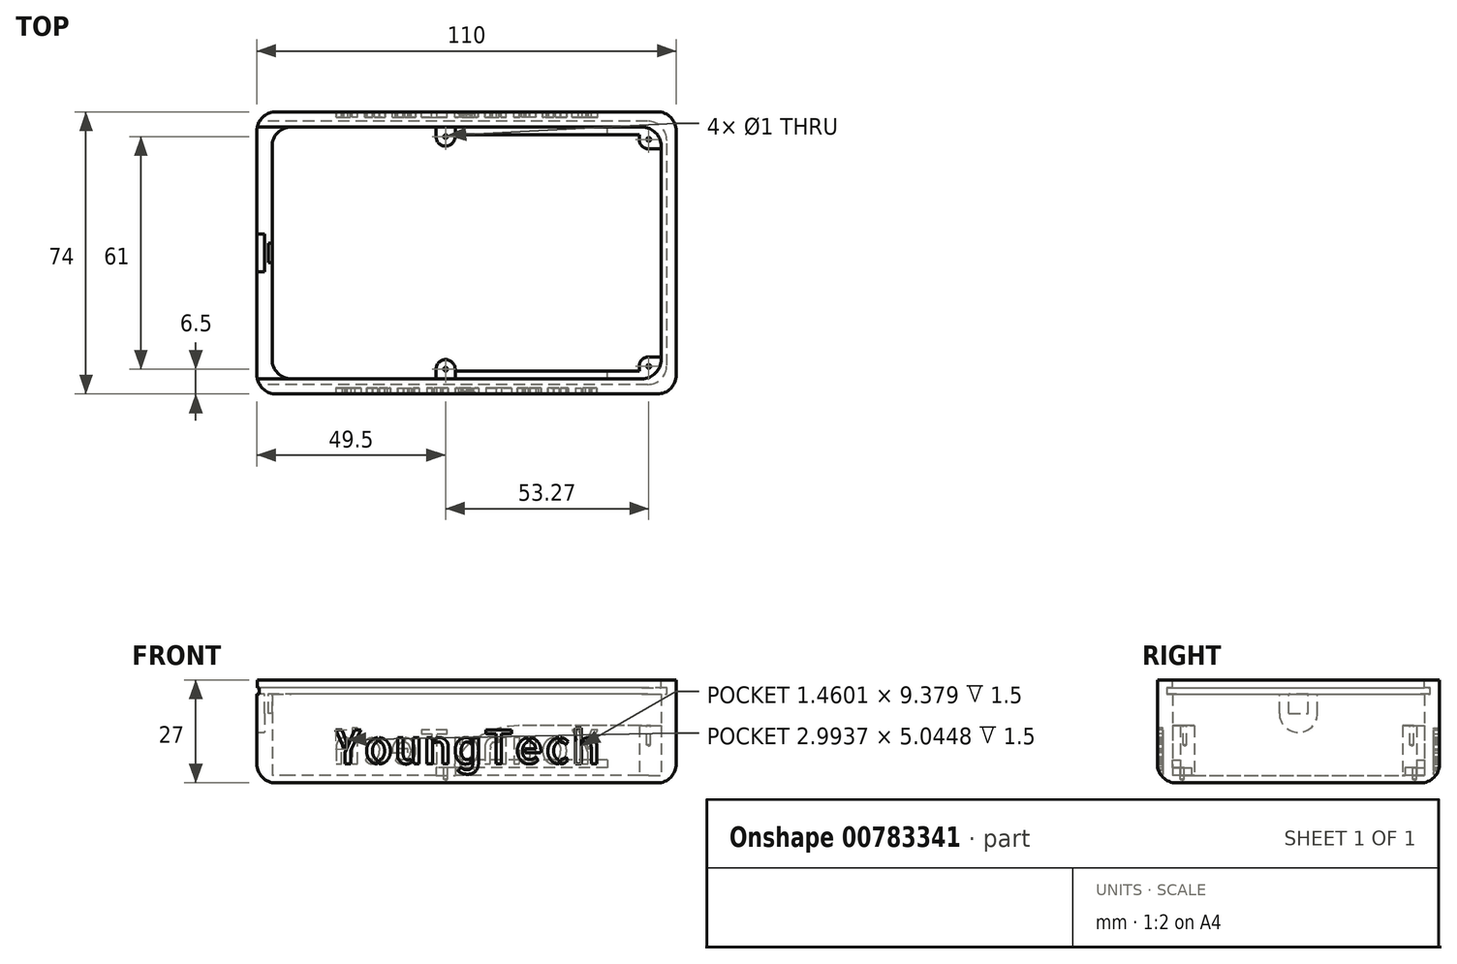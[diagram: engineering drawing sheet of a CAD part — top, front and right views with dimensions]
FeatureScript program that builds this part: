
annotation { "Feature Type Name" : "Feature", "Feature Type Description" : "" }
export const myFeature = defineFeature(function(context is Context, id is Id, definition is map)
    precondition{}
    {
        {
            var Q0;
            Q0=qCreatedBy(makeId("Top.planeOp"),FACE);
            var sketch = newSketch(context, id + "F0", { "sketchPlane" : qUnion([Q0])});
            skLineSegment(sketch, "E0.bottom", {"start": v(55, -37) * mm, "end": v(-55, -37) * mm});
            skLineSegment(sketch, "E0.top", {"start": v(55, 37) * mm, "end": v(-55, 37) * mm});
            skLineSegment(sketch, "E0.left", {"start": v(55, -37) * mm, "end": v(55, 37) * mm});
            skLineSegment(sketch, "E0.right", {"start": v(-55, -37) * mm, "end": v(-55, 37) * mm});
            skPoint(sketch, "E0.middle", {"position": v(0, 0) * mm});
            skSolve(sketch);
        }
        {
            var Q0;
            Q0 = qSketchRegion(id + "F0", true);
            extrude(context, id + "F1", {"entities" : qUnion([Q0]), "depth" : 2 * mm, "offsetDistance" : 25 * mm});
        }
        {
            var Q0;
            Q0=makeQuery(id+"F1.opExtrude","CAP_FACE",FACE,{"disambiguationData":[OSD([sQuery(id+"F0.wireOp",EDGE,"E0.bottom"),sQuery(id+"F0.wireOp",EDGE,"E0.top"),sQuery(id+"F0.wireOp",EDGE,"E0.left"),sQuery(id+"F0.wireOp",EDGE,"E0.right")])],"isStart":false});
            var sketch = newSketch(context, id + "F2", { "sketchPlane" : qUnion([Q0])});
            skLineSegment(sketch, "E1.0.0", {"start": v(55, 37) * mm, "end": v(55, -37) * mm});
            skLineSegment(sketch, "E1.0.1", {"start": v(55, -37) * mm, "end": v(-55, -37) * mm});
            skLineSegment(sketch, "E1.0.2", {"start": v(-55, -37) * mm, "end": v(-55, 37) * mm});
            skLineSegment(sketch, "E1.0.3", {"start": v(-55, 37) * mm, "end": v(55, 37) * mm});
            skLineSegment(sketch, "E2.bottom", {"start": v(51, -33) * mm, "end": v(-51, -33) * mm});
            skLineSegment(sketch, "E2.top", {"start": v(51, 33) * mm, "end": v(-51, 33) * mm});
            skLineSegment(sketch, "E2.left", {"start": v(51, -33) * mm, "end": v(51, 33) * mm});
            skLineSegment(sketch, "E2.right", {"start": v(-51, -33) * mm, "end": v(-51, 33) * mm});
            skPoint(sketch, "E2.middle", {"position": v(0, 0) * mm});
            skSolve(sketch);
        }
        {
            var Q0;
            Q0=makeQuery(id+"F2.imprint","IMPRINT",FACE,{"disambiguationData":[TD([[makeQuery(id+"F2.imprint","IMPRINT",EDGE,{"derivedFrom":sQuery(id+"F2.wireOp",EDGE,"E1.0.0")}),1.0]])]});
            extrude(context, id + "F3", {"entities" : qUnion([Q0]), "operationType" : NewBodyOperationType.ADD, "depth" : 25 * mm, "offsetDistance" : 25 * mm});
        }
        {
            var Q0;
            Q0=makeQuery(id+"F3.boolean.opBoolean","MERGE",EDGE,{"derivedFrom":[makeQuery(id+"F1.opExtrude","SWEPT_EDGE",EDGE,{"disambiguationData":[OSD([sQuery(id+"F0.wireOp",EDGE,"E0.top"),sQuery(id+"F0.wireOp",EDGE,"E0.right")])]}),makeQuery(id+"F3.opExtrude","SWEPT_EDGE",EDGE,{"disambiguationData":[OSD([sQuery(id+"F2.wireOp",EDGE,"E1.0.2"),sQuery(id+"F2.wireOp",EDGE,"E1.0.3")])]})]});
            var Q1;
            Q1=makeQuery(id+"F3.boolean.opBoolean","MERGE",EDGE,{"derivedFrom":[makeQuery(id+"F1.opExtrude","SWEPT_EDGE",EDGE,{"disambiguationData":[OSD([sQuery(id+"F0.wireOp",EDGE,"E0.bottom"),sQuery(id+"F0.wireOp",EDGE,"E0.right")])]}),makeQuery(id+"F3.opExtrude","SWEPT_EDGE",EDGE,{"disambiguationData":[OSD([sQuery(id+"F2.wireOp",EDGE,"E1.0.1"),sQuery(id+"F2.wireOp",EDGE,"E1.0.2")])]})]});
            var Q2;
            Q2=makeQuery(id+"F3.boolean.opBoolean","MERGE",EDGE,{"derivedFrom":[makeQuery(id+"F1.opExtrude","SWEPT_EDGE",EDGE,{"disambiguationData":[OSD([sQuery(id+"F0.wireOp",EDGE,"E0.bottom"),sQuery(id+"F0.wireOp",EDGE,"E0.left")])]}),makeQuery(id+"F3.opExtrude","SWEPT_EDGE",EDGE,{"disambiguationData":[OSD([sQuery(id+"F2.wireOp",EDGE,"E1.0.0"),sQuery(id+"F2.wireOp",EDGE,"E1.0.1")])]})]});
            var Q3;
            Q3=makeQuery(id+"F3.opExtrude","SWEPT_EDGE",EDGE,{"disambiguationData":[OSD([sQuery(id+"F2.wireOp",EDGE,"E2.top"),sQuery(id+"F2.wireOp",EDGE,"E2.left")])]});
            var Q4;
            Q4=makeQuery(id+"F3.boolean.opBoolean","MERGE",EDGE,{"derivedFrom":[makeQuery(id+"F1.opExtrude","SWEPT_EDGE",EDGE,{"disambiguationData":[OSD([sQuery(id+"F0.wireOp",EDGE,"E0.top"),sQuery(id+"F0.wireOp",EDGE,"E0.left")])]}),makeQuery(id+"F3.opExtrude","SWEPT_EDGE",EDGE,{"disambiguationData":[OSD([sQuery(id+"F2.wireOp",EDGE,"E1.0.0"),sQuery(id+"F2.wireOp",EDGE,"E1.0.3")])]})]});
            var Q5;
            Q5=makeQuery(id+"F3.opExtrude","SWEPT_EDGE",EDGE,{"disambiguationData":[OSD([sQuery(id+"F2.wireOp",EDGE,"E2.top"),sQuery(id+"F2.wireOp",EDGE,"E2.right")])]});
            var Q6;
            Q6=makeQuery(id+"F3.opExtrude","SWEPT_EDGE",EDGE,{"disambiguationData":[OSD([sQuery(id+"F2.wireOp",EDGE,"E2.bottom"),sQuery(id+"F2.wireOp",EDGE,"E2.right")])]});
            var Q7;
            Q7=makeQuery(id+"F3.opExtrude","SWEPT_EDGE",EDGE,{"disambiguationData":[OSD([sQuery(id+"F2.wireOp",EDGE,"E2.bottom"),sQuery(id+"F2.wireOp",EDGE,"E2.left")])]});
            fillet(context, id + "F4", {"entities" : qUnion([Q0, Q1, Q2, Q3, Q4, Q5, Q6, Q7]), "radius" : 5 * mm, "tangentPropagation" : true, "allowEdgeOverflow" : false});
        }
        {
            var Q0;
            Q0=makeQuery(id+"F3.boolean.opBoolean","MERGE",FACE,{"derivedFrom":[makeQuery(id+"F1.opExtrude","SWEPT_FACE",FACE,{"disambiguationData":[OSD([sQuery(id+"F0.wireOp",EDGE,"E0.right")])]}),makeQuery(id+"F3.opExtrude","SWEPT_FACE",FACE,{"disambiguationData":[OSD([sQuery(id+"F2.wireOp",EDGE,"E1.0.2")])]})]});
            var sketch = newSketch(context, id + "F5", { "sketchPlane" : qUnion([Q0])});
            skLineSegment(sketch, "E3.top", {"start": v(33, 27) * mm, "end": v(-33, 27) * mm});
            skLineSegment(sketch, "E3.left", {"start": v(33, 25) * mm, "end": v(33, 27) * mm});
            skLineSegment(sketch, "E3.right", {"start": v(-33, 25) * mm, "end": v(-33, 27) * mm});
            skLineSegment(sketch, "E4.bottom", {"start": v(34.5, 23.25) * mm, "end": v(-34.5, 23.25) * mm});
            skLineSegment(sketch, "E4.top", {"start": v(34.5, 25) * mm, "end": v(33, 25) * mm});
            skLineSegment(sketch, "E4.left", {"start": v(34.5, 23.25) * mm, "end": v(34.5, 25) * mm});
            skLineSegment(sketch, "E4.right", {"start": v(-34.5, 23.25) * mm, "end": v(-34.5, 25) * mm});
            skLineSegment(sketch, "E5.trimOffspring", {"start": v(-33, 25) * mm, "end": v(-34.5, 25) * mm});
            skLineSegment(sketch, "E6", {"start": v(0, 27) * mm, "end": v(0, 58.06) * mm, "construction": true});
            skSolve(sketch);
        }
        {
            var Q0;
            Q0 = qSketchRegion(id + "F5", true);
            extrude(context, id + "F6", {"entities" : qUnion([Q0]), "operationType" : NewBodyOperationType.REMOVE, "oppositeDirection" : true, "depth" : 106 * mm, "offsetDistance" : 25 * mm});
        }
        {
            var Q0;
            Q0=makeQuery(id+"F6.boolean.opBoolean","COPY",FACE,{"derivedFrom":makeQuery(id+"F6.opExtrude","SWEPT_FACE",FACE,{"disambiguationData":[OSD([sQuery(id+"F5.wireOp",EDGE,"E4.bottom")])]})});
            var sketch = newSketch(context, id + "F7", { "sketchPlane" : qUnion([Q0])});
            skLineSegment(sketch, "E7", {"start": v(0, 0) * mm, "end": v(-51, 0) * mm, "construction": true});
            skLineSegment(sketch, "E8.bottom", {"start": v(-51, 2.5) * mm, "end": v(-52, 2.5) * mm});
            skLineSegment(sketch, "E8.top", {"start": v(-51, -2.5) * mm, "end": v(-52, -2.5) * mm});
            skLineSegment(sketch, "E8.left", {"start": v(-51, 2.5) * mm, "end": v(-51, -2.5) * mm});
            skLineSegment(sketch, "E8.right", {"start": v(-52, 2.5) * mm, "end": v(-52, -2.5) * mm});
            skSolve(sketch);
        }
        {
            var Q0;
            Q0 = qSketchRegion(id + "F7", true);
            extrude(context, id + "F8", {"entities" : qUnion([Q0]), "operationType" : NewBodyOperationType.REMOVE, "oppositeDirection" : true, "depth" : 5 * mm, "offsetDistance" : 25 * mm});
        }
        {
            var Q0;
            Q0=makeQuery(id+"F6.boolean.opBoolean","COPY",EDGE,{"derivedFrom":makeQuery(id+"F6.opExtrude","CAP_EDGE",EDGE,{"disambiguationData":[OSD([sQuery(id+"F5.wireOp",EDGE,"E3.left")])],"isStart":false})});
            var Q1;
            Q1=makeQuery(id+"F6.boolean.opBoolean","COPY",EDGE,{"derivedFrom":makeQuery(id+"F6.opExtrude","CAP_EDGE",EDGE,{"disambiguationData":[OSD([sQuery(id+"F5.wireOp",EDGE,"E3.right")])],"isStart":false})});
            fillet(context, id + "F9", {"entities" : qUnion([Q0, Q1]), "radius" : 5 * mm, "tangentPropagation" : true, "allowEdgeOverflow" : false});
        }
        {
            var Q0;
            Q0=makeQuery(id+"F6.boolean.opBoolean","MERGE",FACE,{"derivedFrom":[makeQuery(id+"F3.opExtrude","SWEPT_FACE",FACE,{"disambiguationData":[OSD([sQuery(id+"F2.wireOp",EDGE,"E2.left")])]}),makeQuery(id+"F6.opExtrude","CAP_FACE",FACE,{"disambiguationData":[OSD([sQuery(id+"F5.wireOp",EDGE,"E3.top"),sQuery(id+"F5.wireOp",EDGE,"E3.left"),sQuery(id+"F5.wireOp",EDGE,"E3.right"),sQuery(id+"F5.wireOp",EDGE,"E4.bottom"),sQuery(id+"F5.wireOp",EDGE,"E4.top"),sQuery(id+"F5.wireOp",EDGE,"E4.left"),sQuery(id+"F5.wireOp",EDGE,"E4.right"),sQuery(id+"F5.wireOp",EDGE,"E5.trimOffspring")])],"isStart":false})]});
            var sketch = newSketch(context, id + "F10", { "sketchPlane" : qUnion([Q0])});
            skLineSegment(sketch, "E9.0.2", {"start": v(34.5, 25) * mm, "end": v(-34.5, 25) * mm});
            skLineSegment(sketch, "E9.0.3", {"start": v(-34.5, 25) * mm, "end": v(-34.5, 23.25) * mm});
            skLineSegment(sketch, "E9.0.4", {"start": v(-34.5, 23.25) * mm, "end": v(34.5, 23.25) * mm});
            skLineSegment(sketch, "E9.0.9", {"start": v(34.5, 23.25) * mm, "end": v(34.5, 25) * mm});
            skPoint(sketch, "E10.orphan", {"position": v(-28, 25) * mm});
            skPoint(sketch, "E11.orphan", {"position": v(-28, 23.25) * mm});
            skSolve(sketch);
        }
        {
            var Q0;
            Q0 = qSketchRegion(id + "F10", true);
            extrude(context, id + "F11", {"entities" : qUnion([Q0]), "operationType" : NewBodyOperationType.REMOVE, "oppositeDirection" : true, "depth" : 1.5 * mm, "offsetDistance" : 25 * mm});
        }
        {
            var Q0;
            Q0=makeQuery(id+"F11.boolean.opBoolean","COPY",EDGE,{"derivedFrom":makeQuery(id+"F11.opExtrude","CAP_EDGE",EDGE,{"disambiguationData":[OSD([sQuery(id+"F10.wireOp",EDGE,"E9.0.9")])],"isStart":false})});
            var Q1;
            Q1=makeQuery(id+"F11.boolean.opBoolean","COPY",EDGE,{"derivedFrom":makeQuery(id+"F11.opExtrude","CAP_EDGE",EDGE,{"disambiguationData":[OSD([sQuery(id+"F10.wireOp",EDGE,"E9.0.3")])],"isStart":false})});
            fillet(context, id + "F12", {"entities" : qUnion([Q0, Q1]), "radius" : 5 * mm, "tangentPropagation" : true, "allowEdgeOverflow" : false});
        }
        {
            var Q0;
            Q0=makeQuery(id+"F3.boolean.opBoolean","MERGE",FACE,{"derivedFrom":[makeQuery(id+"F1.opExtrude","SWEPT_FACE",FACE,{"disambiguationData":[OSD([sQuery(id+"F0.wireOp",EDGE,"E0.top")])]}),makeQuery(id+"F3.opExtrude","SWEPT_FACE",FACE,{"disambiguationData":[OSD([sQuery(id+"F2.wireOp",EDGE,"E1.0.3")])]})]});
            var sketch = newSketch(context, id + "F13", { "sketchPlane" : qUnion([Q0])});
            skText(sketch, "E12", { "text": "YoungTech", "fontName": "AllertaStencil-Regular.ttf"});
            skLineSegment(sketch, "E13", {"start": v(-50, 0) * mm, "end": v(50, 27) * mm, "construction": true});
            skLineSegment(sketch, "E14", {"start": v(-50, 13.5) * mm, "end": v(50, 13.5) * mm, "construction": true});
            const initialGuessF13  = {"E12": [-0.035, 0.005, 1, 0, 0.0089]};
            skSetInitialGuess(sketch, initialGuessF13);
            skSolve(sketch);
        }
        {
            var Q0;
            Q0 = qSketchRegion(id + "F13", true);
            extrude(context, id + "F14", {"entities" : qUnion([Q0]), "operationType" : NewBodyOperationType.REMOVE, "oppositeDirection" : true, "depth" : 1.5 * mm, "offsetDistance" : 25 * mm});
        }
        {
            var Q0;
            Q0=makeQuery(id+"F3.boolean.opBoolean","MERGE",FACE,{"derivedFrom":[makeQuery(id+"F1.opExtrude","SWEPT_FACE",FACE,{"disambiguationData":[OSD([sQuery(id+"F0.wireOp",EDGE,"E0.bottom")])]}),makeQuery(id+"F3.opExtrude","SWEPT_FACE",FACE,{"disambiguationData":[OSD([sQuery(id+"F2.wireOp",EDGE,"E1.0.1")])]})]});
            var sketch = newSketch(context, id + "F15", { "sketchPlane" : qUnion([Q0])});
            skText(sketch, "E15", { "text": "YoungTech", "fontName": "AllertaStencil-Regular.ttf"});
            skLineSegment(sketch, "E16", {"start": v(-50, 27) * mm, "end": v(50, 0) * mm, "construction": true});
            const initialGuessF15  = {"E15": [-0.035, 0.005, 1, 0, 0.0089]};
            skSetInitialGuess(sketch, initialGuessF15);
            skSolve(sketch);
        }
        {
            var Q0;
            Q0 = qSketchRegion(id + "F15", true);
            extrude(context, id + "F16", {"entities" : qUnion([Q0]), "operationType" : NewBodyOperationType.REMOVE, "oppositeDirection" : true, "depth" : 1.5 * mm, "offsetDistance" : 25 * mm});
        }
        {
            var Q0;
            Q0=makeQuery(id+"F1.opExtrude","CAP_EDGE",EDGE,{"disambiguationData":[OSD([sQuery(id+"F0.wireOp",EDGE,"E0.bottom")])],"isStart":true});
            fillet(context, id + "F17", {"entities" : qUnion([Q0]), "radius" : 5 * mm, "tangentPropagation" : true, "allowEdgeOverflow" : false});
        }
        {
            var Q0;
            Q0=makeQuery(id+"F3.boolean.opBoolean","MERGE",FACE,{"derivedFrom":[makeQuery(id+"F1.opExtrude","SWEPT_FACE",FACE,{"disambiguationData":[OSD([sQuery(id+"F0.wireOp",EDGE,"E0.right")])]}),makeQuery(id+"F3.opExtrude","SWEPT_FACE",FACE,{"disambiguationData":[OSD([sQuery(id+"F2.wireOp",EDGE,"E1.0.2")])]})]});
            var sketch = newSketch(context, id + "F18", { "sketchPlane" : qUnion([Q0])});
            skLineSegment(sketch, "E17.bottom", {"start": v(5, 13.25) * mm, "end": v(-5, 13.25) * mm});
            skLineSegment(sketch, "E17.top", {"start": v(5, 23.25) * mm, "end": v(-5, 23.25) * mm});
            skLineSegment(sketch, "E17.left", {"start": v(5, 13.25) * mm, "end": v(5, 23.25) * mm});
            skLineSegment(sketch, "E17.right", {"start": v(-5, 13.25) * mm, "end": v(-5, 23.25) * mm});
            skPoint(sketch, "E17.middle", {"position": v(0, 18.25) * mm});
            skSolve(sketch);
        }
        {
            var Q0;
            Q0 = qSketchRegion(id + "F18", true);
            extrude(context, id + "F19", {"entities" : qUnion([Q0]), "operationType" : NewBodyOperationType.REMOVE, "oppositeDirection" : true, "depth" : 2 * mm, "offsetDistance" : 25 * mm});
        }
        {
            var Q0;
            Q0=makeQuery(id+"F19.boolean.opBoolean","COPY",EDGE,{"derivedFrom":makeQuery(id+"F19.opExtrude","SWEPT_EDGE",EDGE,{"disambiguationData":[OSD([sQuery(id+"F18.wireOp",EDGE,"E17.bottom"),sQuery(id+"F18.wireOp",EDGE,"E17.right")])]})});
            var Q1;
            Q1=makeQuery(id+"F19.boolean.opBoolean","COPY",EDGE,{"derivedFrom":makeQuery(id+"F19.opExtrude","SWEPT_EDGE",EDGE,{"disambiguationData":[OSD([sQuery(id+"F18.wireOp",EDGE,"E17.bottom"),sQuery(id+"F18.wireOp",EDGE,"E17.left")])]})});
            var Q2;
            Q2=makeQuery(id+"F19.boolean.opBoolean","COPY",EDGE,{"derivedFrom":makeQuery(id+"F19.opExtrude","SWEPT_EDGE",EDGE,{"disambiguationData":[OSD([sQuery(id+"F5.wireOp",EDGE,"E4.bottom"),sQuery(id+"F18.wireOp",EDGE,"E17.top"),sQuery(id+"F18.wireOp",EDGE,"E17.left")])]})});
            var Q3;
            Q3=makeQuery(id+"F19.boolean.opBoolean","COPY",EDGE,{"derivedFrom":makeQuery(id+"F19.opExtrude","SWEPT_EDGE",EDGE,{"disambiguationData":[OSD([sQuery(id+"F5.wireOp",EDGE,"E4.bottom"),sQuery(id+"F18.wireOp",EDGE,"E17.top"),sQuery(id+"F18.wireOp",EDGE,"E17.right")])]})});
            fillet(context, id + "F20", {"entities" : qUnion([Q0, Q1, Q2, Q3]), "radius" : 5 * mm, "tangentPropagation" : true, "allowEdgeOverflow" : false});
        }
        {
            var Q0;
            Q0=makeQuery(id+"F1.opExtrude","CAP_FACE",FACE,{"disambiguationData":[OSD([sQuery(id+"F0.wireOp",EDGE,"E0.bottom"),sQuery(id+"F0.wireOp",EDGE,"E0.top"),sQuery(id+"F0.wireOp",EDGE,"E0.left"),sQuery(id+"F0.wireOp",EDGE,"E0.right")])],"isStart":false});
            var sketch = newSketch(context, id + "F21", { "sketchPlane" : qUnion([Q0])});
            skLineSegment(sketch, "E18", {"start": v(0, 0) * mm, "end": v(65.83, 0) * mm, "construction": true});
            skLineSegment(sketch, "E19.right", {"start": v(-3, 33) * mm, "end": v(-3, 31) * mm});
            skLineSegment(sketch, "E20.MirrorCS", {"start": v(45.27, -31) * mm, "end": v(-3, -31) * mm});
            skLineSegment(sketch, "E21.MirrorCS", {"start": v(-3, -33) * mm, "end": v(-3, -31) * mm});
            skPoint(sketch, "E22.visualSharp", {"position": v(51, 33) * mm});
            skPoint(sketch, "E23.orphan", {"position": v(51, 31) * mm});
            skArc(sketch, "E24.MirrorCS", {"start": v(51, -28) * mm, "mid": v(49.54, -31.54) * mm, "end": v(46, -33) * mm});
            skLineSegment(sketch, "E25", {"start": v(46, -33) * mm, "end": v(-3, -33) * mm});
            skLineSegment(sketch, "E26", {"start": v(46, -28) * mm, "end": v(49.54, -31.54) * mm, "construction": true});
            skArc(sketch, "E27", {"start": v(47.77, -27.27) * mm, "mid": v(46, -28) * mm, "end": v(45.27, -29.77) * mm});
            skLineSegment(sketch, "E28", {"start": v(45.27, -29.77) * mm, "end": v(45.27, -31) * mm});
            skLineSegment(sketch, "E29", {"start": v(47.77, -27.27) * mm, "end": v(51, -27.27) * mm});
            skLineSegment(sketch, "E30", {"start": v(51, -28) * mm, "end": v(51, -27.27) * mm, "construction": true});
            skLineSegment(sketch, "E31.MirrorCS", {"start": v(45.27, 29.77) * mm, "end": v(45.27, 31) * mm});
            skArc(sketch, "E32.MirrorCS", {"start": v(47.77, 27.27) * mm, "mid": v(46, 28) * mm, "end": v(45.27, 29.77) * mm});
            skLineSegment(sketch, "E33.MirrorCS", {"start": v(46, 28) * mm, "end": v(49.54, 31.54) * mm, "construction": true});
            skLineSegment(sketch, "E34.MirrorCS", {"start": v(47.77, 27.27) * mm, "end": v(51, 27.27) * mm});
            skLineSegment(sketch, "E35", {"start": v(51, 28) * mm, "end": v(51, 27.27) * mm});
            skLineSegment(sketch, "E36.MirrorCS", {"start": v(45.27, 31) * mm, "end": v(-3, 31) * mm});
            skArc(sketch, "E37", {"start": v(46, 33) * mm, "mid": v(49.54, 31.54) * mm, "end": v(51, 28) * mm});
            skLineSegment(sketch, "E38", {"start": v(46, 33) * mm, "end": v(-3, 33) * mm});
            skArc(sketch, "E39", {"start": v(-8, 30.5) * mm, "mid": v(-5.5, 28) * mm, "end": v(-3, 30.5) * mm});
            skLineSegment(sketch, "E40", {"start": v(-5.5, 30.5) * mm, "end": v(-5.5, 33) * mm, "construction": true});
            skLineSegment(sketch, "E41", {"start": v(-8, 30.5) * mm, "end": v(-3, 30.5) * mm, "construction": true});
            skLineSegment(sketch, "E42", {"start": v(-3, 31) * mm, "end": v(-3, 30.5) * mm});
            skLineSegment(sketch, "E43", {"start": v(-8, 30.5) * mm, "end": v(-8, 33) * mm});
            skLineSegment(sketch, "E44", {"start": v(-8, 33) * mm, "end": v(-3, 33) * mm});
            skArc(sketch, "E45.MirrorCS", {"start": v(-8, -30.5) * mm, "mid": v(-5.5, -28) * mm, "end": v(-3, -30.5) * mm});
            skLineSegment(sketch, "E46.MirrorCS", {"start": v(-8, -30.5) * mm, "end": v(-8, -33) * mm});
            skLineSegment(sketch, "E47.MirrorCS", {"start": v(-8, -33) * mm, "end": v(-3, -33) * mm});
            skLineSegment(sketch, "E48", {"start": v(-3, -30.5) * mm, "end": v(-3, -31) * mm});
            skSolve(sketch);
        }
        {
            var Q0;
            Q0=makeQuery(id+"F21.imprint","IMPRINT",FACE,{"disambiguationData":[TD([[makeQuery(id+"F21.imprint","IMPRINT",EDGE,{"derivedFrom":sQuery(id+"F21.wireOp",EDGE,"E20.MirrorCS")}),1.0]])]});
            var Q1;
            Q1=makeQuery(id+"F21.imprint","IMPRINT",FACE,{"disambiguationData":[TD([[makeQuery(id+"F21.imprint","IMPRINT",EDGE,{"derivedFrom":sQuery(id+"F21.wireOp",EDGE,"E19.right")}),1.0]])]});
            extrude(context, id + "F22", {"entities" : qUnion([Q0, Q1]), "operationType" : NewBodyOperationType.ADD, "depth" : 13 * mm, "offsetDistance" : 25 * mm});
        }
        {
            var Q0;
            Q0=makeQuery(id+"F22.opExtrude","SWEPT_FACE",FACE,{"disambiguationData":[OSD([sQuery(id+"F21.wireOp",EDGE,"E19.right")])]});
            var sketch = newSketch(context, id + "F23", { "sketchPlane" : qUnion([Q0])});
            skLineSegment(sketch, "E49.bottom", {"start": v(33, 4) * mm, "end": v(-33, 4) * mm});
            skLineSegment(sketch, "E49.top", {"start": v(33, 6) * mm, "end": v(-33, 6) * mm});
            skLineSegment(sketch, "E49.left", {"start": v(33, 4) * mm, "end": v(33, 6) * mm});
            skLineSegment(sketch, "E49.right", {"start": v(-33, 4) * mm, "end": v(-33, 6) * mm});
            skPoint(sketch, "E49.middle", {"position": v(0, 5) * mm});
            skLineSegment(sketch, "E50", {"start": v(-31, 4) * mm, "end": v(-8, 4) * mm, "construction": true});
            skLineSegment(sketch, "E51", {"start": v(0, 2) * mm, "end": v(0, 5) * mm, "construction": true});
            skSolve(sketch);
        }
        {
            var Q0;
            Q0 = qSketchRegion(id + "F23", true);
            extrude(context, id + "F24", {"entities" : qUnion([Q0]), "operationType" : NewBodyOperationType.REMOVE, "oppositeDirection" : true, "depth" : 40 * mm, "offsetDistance" : 25 * mm});
        }
        {
            var Q0;
            Q0=makeQuery(id+"F22.opExtrude","CAP_EDGE",EDGE,{"disambiguationData":[OSD([sQuery(id+"F21.wireOp",EDGE,"E19.right")])],"isStart":false});
            var Q1;
            Q1=makeQuery(id+"F22.opExtrude","CAP_EDGE",EDGE,{"disambiguationData":[OSD([sQuery(id+"F21.wireOp",EDGE,"E21.MirrorCS")])],"isStart":false});
            fillet(context, id + "F25", {"entities" : qUnion([Q0, Q1]), "radius" : 20 * mm, "tangentPropagation" : true, "allowEdgeOverflow" : false});
        }
        {
            var Q0;
            Q0=makeQuery(id+"F22.opExtrude","CAP_FACE",FACE,{"disambiguationData":[OSD([sQuery(id+"F0.wireOp",EDGE,"E0.bottom"),sQuery(id+"F0.wireOp",EDGE,"E0.top"),sQuery(id+"F0.wireOp",EDGE,"E0.left"),sQuery(id+"F0.wireOp",EDGE,"E0.right"),sQuery(id+"F2.wireOp",EDGE,"E2.top"),sQuery(id+"F2.wireOp",EDGE,"E2.left"),sQuery(id+"F21.wireOp",EDGE,"E19.bottom"),sQuery(id+"F21.wireOp",EDGE,"E19.top"),sQuery(id+"F21.wireOp",EDGE,"E19.left"),sQuery(id+"F21.wireOp",EDGE,"E19.right")])],"isStart":false});
            var sketch = newSketch(context, id + "F26", { "sketchPlane" : qUnion([Q0])});
            skLineSegment(sketch, "E52", {"start": v(0, 0) * mm, "end": v(38.34, 0) * mm, "construction": true});
            skSolve(sketch);
        }
        {
            var Q0;
            Q0=makeQuery(id+"F21.imprint","IMPRINT",FACE,{"disambiguationData":[TD([[makeQuery(id+"F21.imprint","IMPRINT",EDGE,{"derivedFrom":sQuery(id+"F21.wireOp",EDGE,"E19.right")}),-1.0]])]});
            var Q1;
            Q1=makeQuery(id+"F21.imprint","IMPRINT",FACE,{"disambiguationData":[TD([[makeQuery(id+"F21.imprint","IMPRINT",EDGE,{"derivedFrom":sQuery(id+"F21.wireOp",EDGE,"E21.MirrorCS")}),1.0]])]});
            extrude(context, id + "F27", {"entities" : qUnion([Q0, Q1]), "operationType" : NewBodyOperationType.ADD, "depth" : 2 * mm, "offsetDistance" : 25 * mm});
        }
        {
            var Q0;
            {var subQ0=sQuery(id+"F21.wireOp",EDGE,"E19.right");var subQ2=sQuery(id+"F23.wireOp",EDGE,"E49.bottom");Q0=makeQuery(id+"F27.boolean.opBoolean","MERGE",FACE,{"derivedFrom":[makeQuery(id+"F24.boolean.opBoolean","COPY",FACE,{"disambiguationData":[TD([makeQuery(id+"F3.opExtrude","SWEPT_FACE",FACE,{"disambiguationData":[OSD([sQuery(id+"F2.wireOp",EDGE,"E2.top")])]})])],"derivedFrom":makeQuery(id+"F24.opExtrude","SWEPT_FACE",FACE,{"disambiguationData":[OSD([subQ2])]})}),makeQuery(id+"F27.opExtrude","CAP_FACE",FACE,{"disambiguationData":[OSD([subQ0,sQuery(id+"F21.wireOp",EDGE,"E39"),sQuery(id+"F21.wireOp",EDGE,"E42"),sQuery(id+"F21.wireOp",EDGE,"E43"),sQuery(id+"F21.wireOp",EDGE,"E44")])],"isStart":false})]});}
            var sketch = newSketch(context, id + "F28", { "sketchPlane" : qUnion([Q0])});
            skPoint(sketch, "E53", {"position": v(-5.5, 30.5) * mm});
            skSolve(sketch);
        }
        {
            var Q0;
            {var subQ0=sQuery(id+"F21.wireOp",EDGE,"E21.MirrorCS");var subQ2=sQuery(id+"F23.wireOp",EDGE,"E49.bottom");Q0=makeQuery(id+"F27.boolean.opBoolean","MERGE",FACE,{"derivedFrom":[makeQuery(id+"F24.boolean.opBoolean","COPY",FACE,{"disambiguationData":[TD([makeQuery(id+"F3.opExtrude","SWEPT_FACE",FACE,{"disambiguationData":[OSD([sQuery(id+"F2.wireOp",EDGE,"E2.bottom")])]})])],"derivedFrom":makeQuery(id+"F24.opExtrude","SWEPT_FACE",FACE,{"disambiguationData":[OSD([subQ2])]})}),makeQuery(id+"F27.opExtrude","CAP_FACE",FACE,{"disambiguationData":[OSD([subQ0,sQuery(id+"F21.wireOp",EDGE,"E45.MirrorCS"),sQuery(id+"F21.wireOp",EDGE,"E46.MirrorCS"),sQuery(id+"F21.wireOp",EDGE,"E47.MirrorCS"),sQuery(id+"F21.wireOp",EDGE,"E48")])],"isStart":false})]});}
            var sketch = newSketch(context, id + "F29", { "sketchPlane" : qUnion([Q0])});
            skPoint(sketch, "E54", {"position": v(-5.5, -30.5) * mm});
            skSolve(sketch);
        }
        {
            var Q0;
            Q0=sQuery(id+"F28.wireOp",VERTEX,"E53");
            var Q1;
            Q1=sQuery(id+"F29.wireOp",VERTEX,"E54");
            var Q2;
            Q2=makeQuery(id+"F1.opExtrude","SWEPT_BODY",BODY,{"disambiguationData":[OSD([sQuery(id+"F0.wireOp",EDGE,"E0.bottom"),sQuery(id+"F0.wireOp",EDGE,"E0.top"),sQuery(id+"F0.wireOp",EDGE,"E0.left"),sQuery(id+"F0.wireOp",EDGE,"E0.right")])]});
            hole(context, id + "F30", {"style" : HoleStyle.SIMPLE, "endStyle" : HoleEndStyle.BLIND, "holeDiameter" : 1 * mm, "majorDiameter" : 5 * mm, "holeDepth" : 3 * mm, "isTappedThrough" : true, "tappedDepth" : 12 * mm, "tapClearance" : 3, "startFromSketch" : true, "locations" : qUnion([Q0, Q1]), "scope" : qUnion([Q2])});
        }
        {
            var Q0;
            {var subQ4=sQuery(id+"F21.wireOp",EDGE,"E31.MirrorCS");Q0=makeQuery(id+"F26.imprint","IMPRINT",FACE,{"disambiguationData":[TD([[makeQuery(id+"F26.imprint","IMPRINT",EDGE,{"derivedFrom":makeQuery(id+"F22.opExtrude","CAP_EDGE",EDGE,{"disambiguationData":[OSD([subQ4])],"isStart":false})}),-1.0]])]});}
            var sketch = newSketch(context, id + "F31", { "sketchPlane" : qUnion([Q0])});
            skLineSegment(sketch, "E55", {"start": v(47.77, 29.77) * mm, "end": v(47.77, -29.77) * mm, "construction": true});
            skSolve(sketch);
        }
        {
            var Q0;
            Q0=sQuery(id+"F31.wireOp",VERTEX,"E55.start");
            var Q1;
            Q1=sQuery(id+"F31.wireOp",VERTEX,"E55.end");
            var Q2;
            Q2=makeQuery(id+"F1.opExtrude","SWEPT_BODY",BODY,{"disambiguationData":[OSD([sQuery(id+"F0.wireOp",EDGE,"E0.bottom"),sQuery(id+"F0.wireOp",EDGE,"E0.top"),sQuery(id+"F0.wireOp",EDGE,"E0.left"),sQuery(id+"F0.wireOp",EDGE,"E0.right")])]});
            hole(context, id + "F32", {"style" : HoleStyle.SIMPLE, "endStyle" : HoleEndStyle.BLIND, "holeDiameter" : 1 * mm, "majorDiameter" : 5 * mm, "holeDepth" : 5 * mm, "isTappedThrough" : true, "tappedDepth" : 12 * mm, "tapClearance" : 3, "startFromSketch" : true, "locations" : qUnion([Q0, Q1]), "scope" : qUnion([Q2])});
        }
    });
